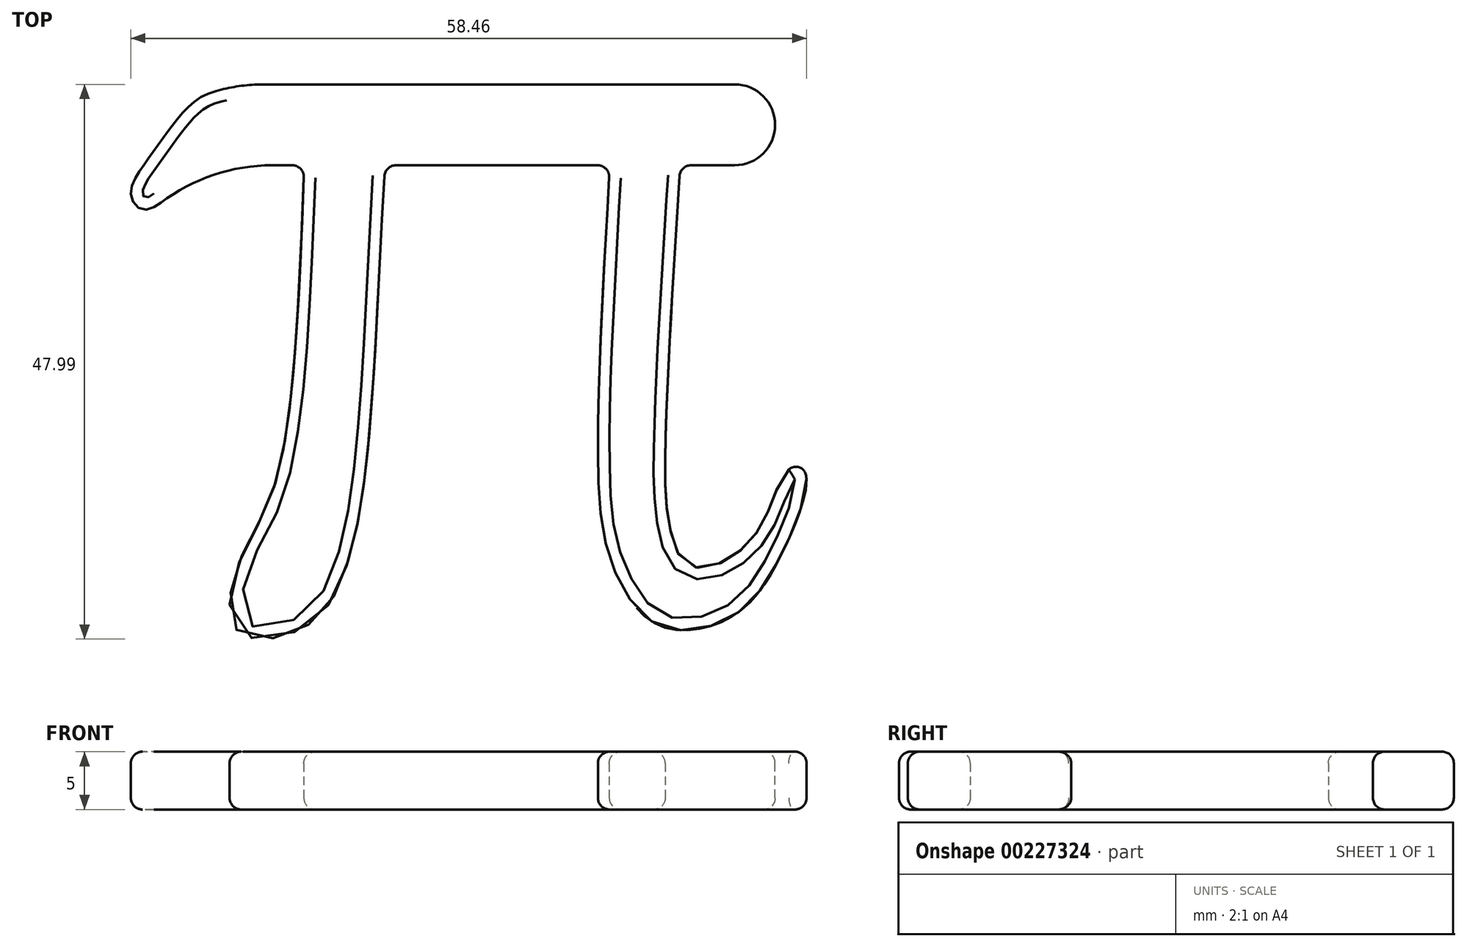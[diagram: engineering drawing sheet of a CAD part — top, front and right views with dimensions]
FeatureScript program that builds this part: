
annotation { "Feature Type Name" : "Feature", "Feature Type Description" : "" }
export const myFeature = defineFeature(function(context is Context, id is Id, definition is map)
    precondition{}
    {
        {
            var Q0;
            Q0=qCreatedBy(makeId("Top.planeOp"),FACE);
            var sketch = newSketch(context, id + "F0", { "sketchPlane" : qUnion([Q0])});
            skLineSegment(sketch, "E0.bottom", {"start": v(2.56, 0) * mm, "end": v(50, 0) * mm});
            skLineSegment(sketch, "E0.top", {"start": v(4.24, 7) * mm, "end": v(50, 7) * mm});
            skLineSegment(sketch, "E0.right", {"start": v(50, 0) * mm, "end": v(50, 7) * mm});
            skFitSpline(sketch, "E1", {"points": [v(9.27, 0) * mm, v(6.67, -27.82) * mm, v(3.68, -34.2) * mm, v(3.48, -40.3) * mm, v(9.07, -40.1) * mm, v(12.46, -35.9) * mm, v(14.46, -27.33) * mm, v(15.75, -9.37) * mm, v(16.25, 0) * mm], "startDerivative": vector(-6.02, -160.43) * mm, "endDerivative": vector(3.75, 68.71) * mm});
            skFitSpline(sketch, "E2", {"points": [v(35.7, 0) * mm, v(34.8, -29.02) * mm, v(36.4, -35.7) * mm, v(40, -39.84) * mm, v(46.04, -39.18) * mm, v(50.47, -33.8) * mm, v(52.57, -26.53) * mm, v(51.17, -26.33) * mm, v(48.25, -32.01) * mm, v(42.8, -34.72) * mm, v(40.9, -31.42) * mm, v(40.5, -25.53) * mm, v(41, -13.06) * mm, v(41.8, 0) * mm], "startDerivative": vector(-12.57, -223.41) * mm, "endDerivative": vector(8.2, 125.81) * mm});
            skFitSpline(sketch, "E3", {"points": [v(4.24, 7) * mm, v(0.66, 6.06) * mm, v(-1.75, 3.93) * mm, v(-4.22, 0.57) * mm, v(-5.73, -2.56) * mm, v(-4.44, -3.85) * mm, v(-0.91, -1.39) * mm, v(2.56, 0) * mm], "startDerivative": vector(-25, -5.66) * mm, "endDerivative": vector(23.33, 5.56) * mm});
            skPoint(sketch, "E4.orphan", {"position": v(0, 0) * mm});
            skSolve(sketch);
        }
        {
            var Q0;
            Q0 = qSketchRegion(id + "F0", true);
            extrude(context, id + "F1", {"entities" : qUnion([Q0]), "depth" : 5 * mm});
        }
        {
            var Q0;
            Q0=makeQuery(id+"F1.opExtrude","SWEPT_EDGE",EDGE,{"disambiguationData":[OSD([sQuery(id+"F0.wireOp",EDGE,"E0.top"),sQuery(id+"F0.wireOp",EDGE,"E3")])]});
            var Q1;
            Q1=makeQuery(id+"F1.opExtrude","SWEPT_EDGE",EDGE,{"disambiguationData":[OSD([sQuery(id+"F0.wireOp",EDGE,"E0.bottom"),sQuery(id+"F0.wireOp",EDGE,"E3")])]});
            fillet(context, id + "F2", {"entities" : qUnion([Q0, Q1]), "radius" : 16 * mm, "tangentPropagation" : true, "allowEdgeOverflow" : false});
        }
        {
            var Q0;
            {var subQ0=sQuery(id+"F0.wireOp",EDGE,"E1");var subQ1=sQuery(id+"F0.wireOp",EDGE,"E0.bottom");Q0=makeQuery(id+"F1.opExtrude","SWEPT_EDGE",EDGE,{"disambiguationData":[OSD([subQ1,subQ0]),TDD([makeQuery(id+"F0.imprint","INTERSECT",VERTEX,{"disambiguationData":[OD(0.0)],"derivedFrom":[subQ1,subQ0]})])]});}
            var Q1;
            {var subQ0=sQuery(id+"F0.wireOp",EDGE,"E1");var subQ1=sQuery(id+"F0.wireOp",EDGE,"E0.bottom");Q1=makeQuery(id+"F1.opExtrude","SWEPT_EDGE",EDGE,{"disambiguationData":[OSD([subQ1,subQ0]),TDD([makeQuery(id+"F0.imprint","INTERSECT",VERTEX,{"disambiguationData":[OD(1.0)],"derivedFrom":[subQ1,subQ0]})])]});}
            var Q2;
            {var subQ0=sQuery(id+"F0.wireOp",EDGE,"E2");var subQ1=sQuery(id+"F0.wireOp",EDGE,"E0.bottom");Q2=makeQuery(id+"F1.opExtrude","SWEPT_EDGE",EDGE,{"disambiguationData":[OSD([subQ1,subQ0]),TDD([makeQuery(id+"F0.imprint","INTERSECT",VERTEX,{"disambiguationData":[OD(1.0)],"derivedFrom":[subQ1,subQ0]})])]});}
            var Q3;
            {var subQ0=sQuery(id+"F0.wireOp",EDGE,"E2");var subQ1=sQuery(id+"F0.wireOp",EDGE,"E0.bottom");Q3=makeQuery(id+"F1.opExtrude","SWEPT_EDGE",EDGE,{"disambiguationData":[OSD([subQ1,subQ0]),TDD([makeQuery(id+"F0.imprint","INTERSECT",VERTEX,{"disambiguationData":[OD(0.0)],"derivedFrom":[subQ1,subQ0]})])]});}
            fillet(context, id + "F3", {"entities" : qUnion([Q0, Q1, Q2, Q3]), "radius" : 1 * mm, "tangentPropagation" : true, "allowEdgeOverflow" : false});
        }
        {
            var Q0;
            Q0=makeQuery(id+"F1.opExtrude","SWEPT_EDGE",EDGE,{"disambiguationData":[OSD([sQuery(id+"F0.wireOp",EDGE,"E0.top"),sQuery(id+"F0.wireOp",EDGE,"E0.right")])]});
            var Q1;
            Q1=makeQuery(id+"F1.opExtrude","SWEPT_EDGE",EDGE,{"disambiguationData":[OSD([sQuery(id+"F0.wireOp",EDGE,"E0.bottom"),sQuery(id+"F0.wireOp",EDGE,"E0.right")])]});
            fillet(context, id + "F4", {"entities" : qUnion([Q0, Q1]), "radius" : 3.5 * mm, "tangentPropagation" : true, "allowEdgeOverflow" : false});
        }
        {
            var Q0;
            Q0=makeQuery(id+"F1.opExtrude","CAP_FACE",FACE,{"disambiguationData":[OSD([sQuery(id+"F0.wireOp",EDGE,"E0.bottom"),sQuery(id+"F0.wireOp",EDGE,"E0.top"),sQuery(id+"F0.wireOp",EDGE,"E0.right"),sQuery(id+"F0.wireOp",EDGE,"E1"),sQuery(id+"F0.wireOp",EDGE,"E2"),sQuery(id+"F0.wireOp",EDGE,"E3")])],"isStart":false});
            var Q1;
            Q1=makeQuery(id+"F1.opExtrude","CAP_FACE",FACE,{"disambiguationData":[OSD([sQuery(id+"F0.wireOp",EDGE,"E0.bottom"),sQuery(id+"F0.wireOp",EDGE,"E0.top"),sQuery(id+"F0.wireOp",EDGE,"E0.right"),sQuery(id+"F0.wireOp",EDGE,"E1"),sQuery(id+"F0.wireOp",EDGE,"E2"),sQuery(id+"F0.wireOp",EDGE,"E3")])],"isStart":true});
            fillet(context, id + "F5", {"entities" : qUnion([Q0, Q1]), "radius" : 1 * mm, "tangentPropagation" : true, "allowEdgeOverflow" : false});
        }
    });
